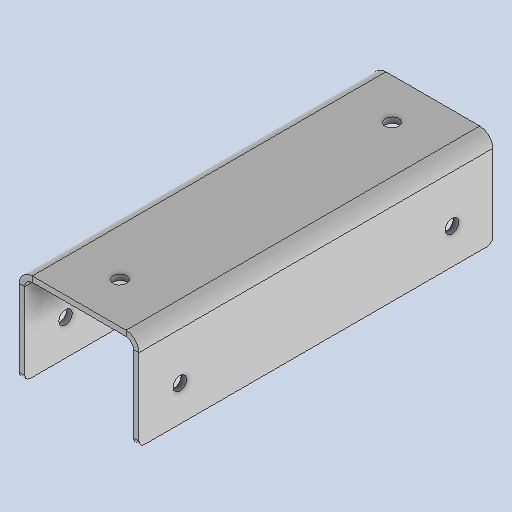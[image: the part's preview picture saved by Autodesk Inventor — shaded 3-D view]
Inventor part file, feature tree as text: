
AUTODESK INVENTOR PART (.ipt)
format: ipt  version: 2025 (Build 290162010, 162A)  size: 313,344 bytes
history: native  units: mm
features: sheet_metal_op x4, sketch x4, other x3, extrude x2, fillet x1, pattern_linear x1
ambient origin geometry x8: Origin, YZ Plane, XZ Plane, XY Plane, X Axis, Y Axis, Z Axis, Center Point
bodies: Solid1 (feature_tree)
feature tree (15):
  sheet_metal_op  "Face1"
  sheet_metal_op  "Flange1"
  extrude  "Extrusion1"  Depth=130.0mm
  sketch  "Sketch6"  dims[d6=2.75mm d7=35.0mm d8=90.0deg d9=2.75mm d10=8.0mm d11=2.0mm d12=2.75mm d14=0.0mm d15=13.0mm d17=2.5mm d18=15.0mm d19=0.0mm d20=0.0mm d26=2.0mm d27=5.0mm d28=10.0mm d29=0.0mm d30=20.0mm d32=100.0mm]
  extrude  "Extrusion3"  Depth=2.0mm
  fillet  "Fillet1"  Radius=1.0mm
  pattern_linear  "Rectangular Pattern2"  Spacing1=35.0mm  [1 undecoded]
  sketch  "Sketch1"  dims[d0=40.0mm d1=130.0mm]
  other  "Plate1"
  sketch  "Sketch2"  dims[d2=2.0mm d3=2.0mm d4=1.0mm]
  other  "Plate2"
  sheet_metal_op  "Bend1"
  sheet_metal_op  "Corner1"
  sketch  "Sketch3"  dims[d5=4.0mm]
  other  "Definition1"
note: 1 required parameter value undecoded (feature->parameter linkage not recoverable at this tier; creation-order binding heuristic only, values carry confidence <= 0.55)
